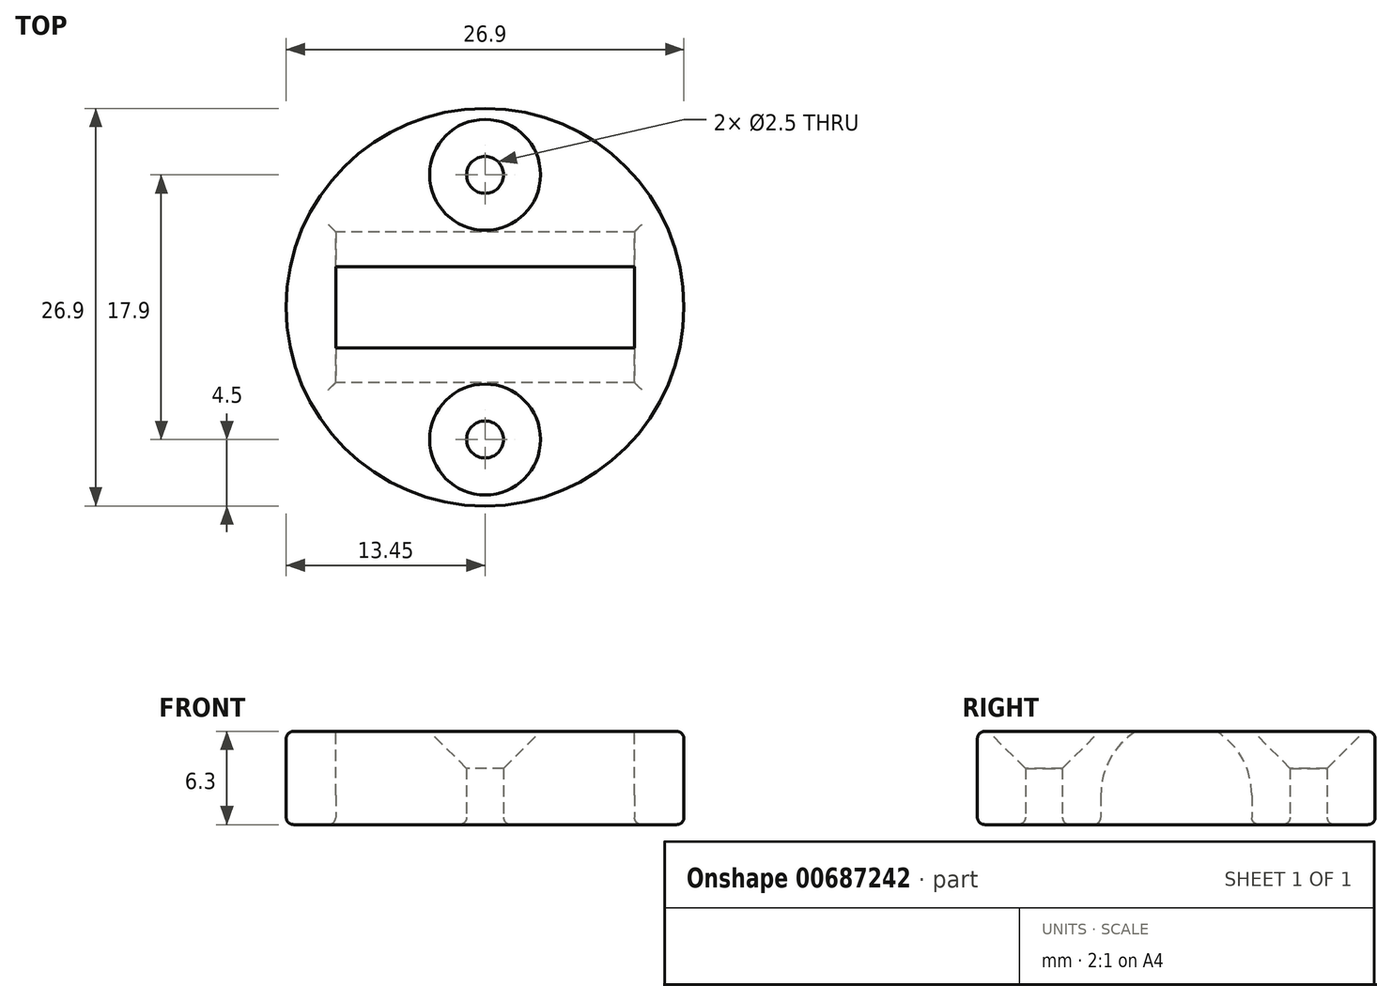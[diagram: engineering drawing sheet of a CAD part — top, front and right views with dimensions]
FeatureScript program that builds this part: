
annotation { "Feature Type Name" : "Feature", "Feature Type Description" : "" }
export const myFeature = defineFeature(function(context is Context, id is Id, definition is map)
    precondition{}
    {
        {
            var Q0;
            Q0=qCreatedBy(makeId("Top.planeOp"),FACE);
            var sketch = newSketch(context, id + "F0", { "sketchPlane" : qUnion([Q0])});
            skCircle(sketch, "E0", {"center": v(0, 0) * mm, "radius": 13.45 * mm});
            skSolve(sketch);
        }
        {
            var Q0;
            Q0=qSketchRegion(id+"F0",true);
            extrude(context, id + "F1", {"entities" : qUnion([Q0]), "depth" : 6.3 * mm, "offsetDistance" : 25 * mm});
        }
        {
            var Q0;
            Q0=qCreatedBy(makeId("Right.planeOp"),FACE);
            var sketch = newSketch(context, id + "F2", { "sketchPlane" : qUnion([Q0])});
            skArc(sketch, "E1", {"start": v(5.1, 2) * mm, "mid": v(0, 7.1) * mm, "end": v(-5.1, 2) * mm});
            skLineSegment(sketch, "E2", {"start": v(5.1, 2) * mm, "end": v(5.1, 0) * mm});
            skLineSegment(sketch, "E3", {"start": v(-5.1, 2) * mm, "end": v(-5.1, 0) * mm});
            skLineSegment(sketch, "E4", {"start": v(-5.1, 0) * mm, "end": v(5.1, 0) * mm});
            skSolve(sketch);
        }
        {
            var Q0;
            Q0=qSketchRegion(id+"F2",true);
            extrude(context, id + "F3", {"entities" : qUnion([Q0]), "operationType" : NewBodyOperationType.REMOVE, "depth" : 10.1 * mm, "offsetDistance" : 25 * mm, "hasSecondDirection" : true, "secondDirectionOppositeDirection" : true, "secondDirectionDepth" : 10.1 * mm});
        }
        {
            var Q0;
            Q0=makeQuery(id+"F1.opExtrude","CAP_FACE",FACE,{"disambiguationData":[OSD([sQuery(id+"F0.wireOp",EDGE,"E0")])],"isStart":true});
            var sketch = newSketch(context, id + "F4", { "sketchPlane" : qUnion([Q0])});
            skCircle(sketch, "E5", {"center": v(0, 8.95) * mm, "radius": 1.25 * mm});
            skPoint(sketch, "E5.centerSnap0", {"position": v(0, 4.9) * mm});
            skCircle(sketch, "E6.MirrorC", {"center": v(0, -8.95) * mm, "radius": 1.25 * mm});
            skSolve(sketch);
        }
        {
            var Q0;
            Q0=qSketchRegion(id+"F4",true);
            extrude(context, id + "F5", {"entities" : qUnion([Q0]), "operationType" : NewBodyOperationType.REMOVE, "oppositeDirection" : true, "depth" : 10 * mm, "offsetDistance" : 25 * mm});
        }
        {
            var Q0;
            Q0=makeQuery(id+"F1.opExtrude","CAP_FACE",FACE,{"disambiguationData":[OSD([sQuery(id+"F0.wireOp",EDGE,"E0")])],"isStart":true});
            var Q1;
            Q1=makeQuery(id+"F1.opExtrude","CAP_EDGE",EDGE,{"disambiguationData":[OSD([sQuery(id+"F0.wireOp",EDGE,"E0")])],"isStart":false});
            fillet(context, id + "F6", {"entities" : qUnion([Q0, Q1]), "radius" : .5 * mm, "tangentPropagation" : true, "allowEdgeOverflow" : false});
        }
        {
            var Q0;
            Q0=makeQuery(id+"F5.boolean.opBoolean","INTERSECT",EDGE,{"derivedFrom":[makeQuery(id+"F1.opExtrude","CAP_FACE",FACE,{"disambiguationData":[OSD([sQuery(id+"F0.wireOp",EDGE,"E0")])],"isStart":false}),makeQuery(id+"F5.opExtrude","SWEPT_FACE",FACE,{"disambiguationData":[OSD([sQuery(id+"F4.wireOp",EDGE,"E5")])]})]});
            var Q1;
            Q1=makeQuery(id+"F5.boolean.opBoolean","INTERSECT",EDGE,{"derivedFrom":[makeQuery(id+"F1.opExtrude","CAP_FACE",FACE,{"disambiguationData":[OSD([sQuery(id+"F0.wireOp",EDGE,"E0")])],"isStart":false}),makeQuery(id+"F5.opExtrude","SWEPT_FACE",FACE,{"disambiguationData":[OSD([sQuery(id+"F4.wireOp",EDGE,"E6.MirrorC")])]})]});
            chamfer(context, id + "F7", {"entities" : qUnion([Q0, Q1]), "width" : 2.5 * mm, "tangentPropagation" : true});
        }
    });
